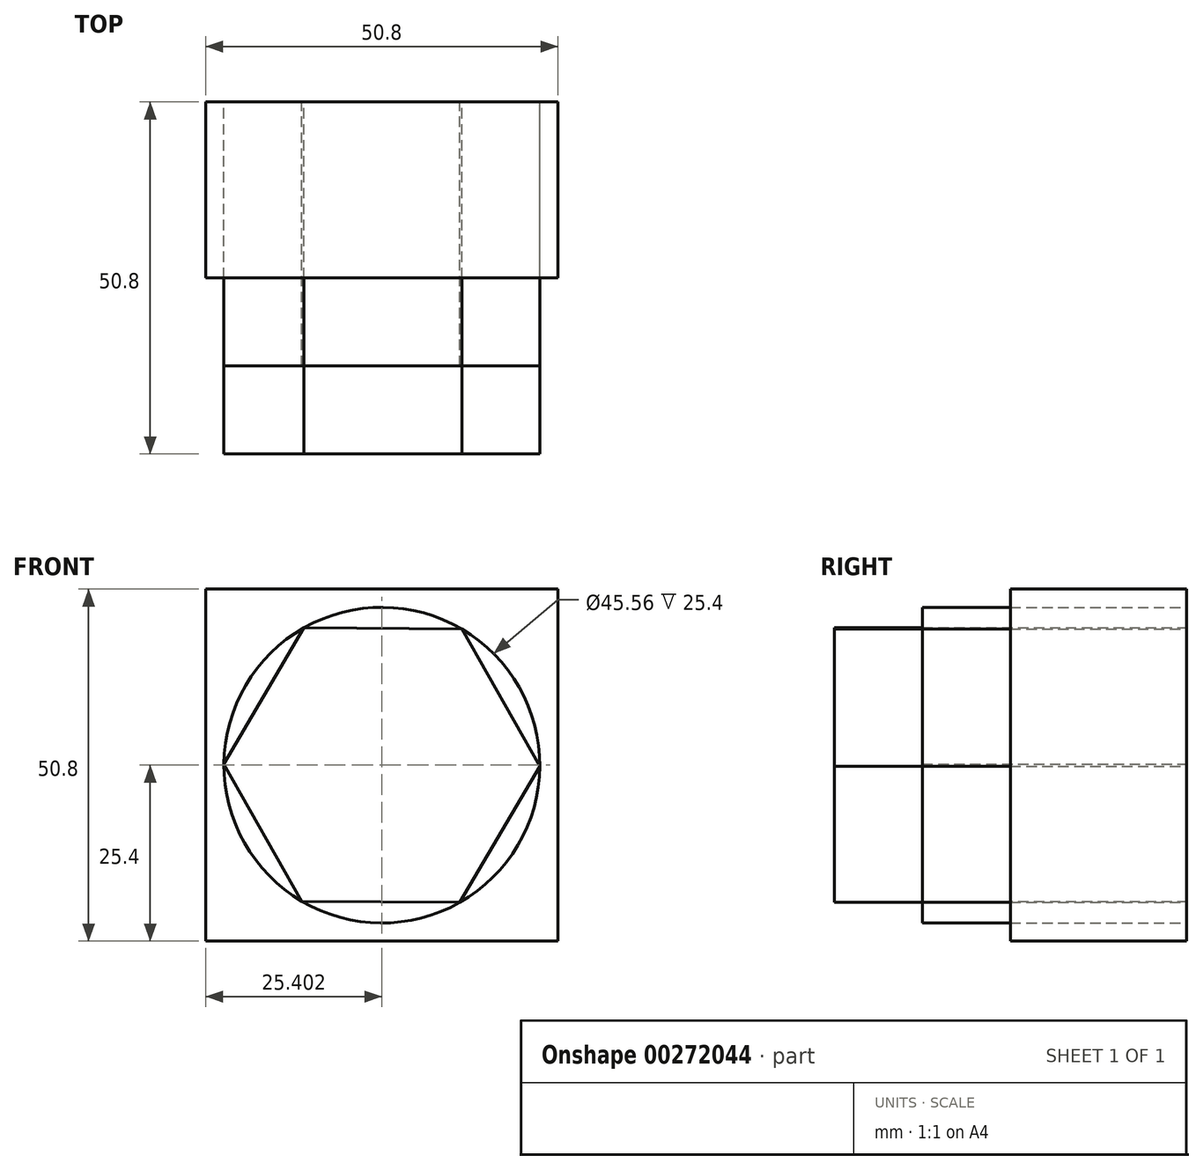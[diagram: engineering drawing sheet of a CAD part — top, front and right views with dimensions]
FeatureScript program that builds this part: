
annotation { "Feature Type Name" : "Feature", "Feature Type Description" : "" }
export const myFeature = defineFeature(function(context is Context, id is Id, definition is map)
    precondition{}
    {
        {
            var Q0;
            Q0=qCreatedBy(makeId("Front.planeOp"),FACE);
            var sketch = newSketch(context, id + "F0", { "sketchPlane" : qUnion([Q0])});
            skLineSegment(sketch, "E0.bottom", {"start": v(-36.5, 21.67) * mm, "end": v(14.3, 21.67) * mm});
            skLineSegment(sketch, "E0.top", {"start": v(-36.5, -29.13) * mm, "end": v(14.3, -29.13) * mm});
            skLineSegment(sketch, "E0.left", {"start": v(-36.5, 21.67) * mm, "end": v(-36.5, -29.13) * mm});
            skLineSegment(sketch, "E0.right", {"start": v(14.3, 21.67) * mm, "end": v(14.3, -29.13) * mm});
            skLineSegment(sketch, "E1", {"start": v(-11.1, 21.67) * mm, "end": v(-11.1, 19.05) * mm});
            skLineSegment(sketch, "E2", {"start": v(-36.5, -3.73) * mm, "end": v(-33.89, -3.73) * mm});
            skCircle(sketch, "E3", {"center": v(-11.1, -3.73) * mm, "radius": 22.78 * mm});
            skLineSegment(sketch, "E4.trimOffspring", {"start": v(-11.1, -26.5) * mm, "end": v(-11.1, -29.13) * mm});
            skLineSegment(sketch, "E5.trimOffspring", {"start": v(11.67, -3.73) * mm, "end": v(14.3, -3.73) * mm});
            skCircle(sketch, "E6.cCircle", {"center": v(-11.1, -3.73) * mm, "radius": 22.78 * mm, "construction": true});
            skLineSegment(sketch, "E6.0", {"start": v(-22.34, 16.09) * mm, "end": v(0.44, 15.9) * mm});
            skLineSegment(sketch, "E6.1", {"start": v(0.44, 15.9) * mm, "end": v(11.67, -3.9) * mm});
            skLineSegment(sketch, "E6.2", {"start": v(11.67, -3.9) * mm, "end": v(0.13, -23.55) * mm});
            skLineSegment(sketch, "E6.3", {"start": v(0.13, -23.55) * mm, "end": v(-22.65, -23.37) * mm});
            skLineSegment(sketch, "E6.4", {"start": v(-22.65, -23.37) * mm, "end": v(-33.89, -3.55) * mm});
            skLineSegment(sketch, "E6.5", {"start": v(-33.89, -3.55) * mm, "end": v(-22.34, 16.09) * mm});
            skSolve(sketch);
        }
        {
            var Q0;
            {var subQ3=sQuery(id+"F0.wireOp",EDGE,"E1");Q0=makeQuery(id+"F0.imprint","IMPRINT",FACE,{"disambiguationData":[TD([[makeQuery(id+"F0.imprint","IMPRINT",EDGE,{"derivedFrom":subQ3}),1.0]])]});}
            var Q1;
            {var subQ1=sQuery(id+"F0.wireOp",EDGE,"E1");Q1=makeQuery(id+"F0.imprint","IMPRINT",FACE,{"disambiguationData":[TD([[makeQuery(id+"F0.imprint","IMPRINT",EDGE,{"derivedFrom":subQ1}),-1.0]])]});}
            var Q2;
            {var subQ1=sQuery(id+"F0.wireOp",EDGE,"E2");Q2=makeQuery(id+"F0.imprint","IMPRINT",FACE,{"disambiguationData":[TD([[makeQuery(id+"F0.imprint","IMPRINT",EDGE,{"derivedFrom":subQ1}),-1.0]])]});}
            var Q3;
            {var subQ8=sQuery(id+"F0.wireOp",EDGE,"E4.trimOffspring");Q3=makeQuery(id+"F0.imprint","IMPRINT",FACE,{"disambiguationData":[TD([[makeQuery(id+"F0.imprint","IMPRINT",EDGE,{"derivedFrom":subQ8}),1.0]])]});}
            extrude(context, id + "F1", {"entities" : qUnion([Q0, Q1, Q2, Q3]), "depth" : 25.4 * mm});
        }
        {
            var Q0;
            Q0=makeQuery(id+"F0.imprint","IMPRINT",FACE,{"disambiguationData":[TD([[makeQuery(id+"F0.imprint","IMPRINT",EDGE,{"derivedFrom":sQuery(id+"F0.wireOp",EDGE,"E6.0")}),-1.0]])]});
            extrude(context, id + "F2", {"entities" : qUnion([Q0]), "operationType" : NewBodyOperationType.ADD, "depth" : 50.8 * mm});
        }
        {
            var Q0;
            {var subQ0=sQuery(id+"F0.wireOp",EDGE,"E6.5");Q0=makeQuery(id+"F0.imprint","IMPRINT",FACE,{"disambiguationData":[TD([[makeQuery(id+"F0.imprint","IMPRINT",EDGE,{"derivedFrom":subQ0}),1.0]])]});}
            var Q1;
            {var subQ2=sQuery(id+"F0.wireOp",EDGE,"E6.1");Q1=makeQuery(id+"F0.imprint","IMPRINT",FACE,{"disambiguationData":[TD([[makeQuery(id+"F0.imprint","IMPRINT",EDGE,{"derivedFrom":subQ2}),1.0]])]});}
            var Q2;
            {var subQ2=sQuery(id+"F0.wireOp",EDGE,"E6.0");Q2=makeQuery(id+"F0.imprint","IMPRINT",FACE,{"disambiguationData":[TD([[makeQuery(id+"F0.imprint","IMPRINT",EDGE,{"derivedFrom":subQ2}),1.0]])]});}
            var Q3;
            {var subQ2=sQuery(id+"F0.wireOp",EDGE,"E6.4");Q3=makeQuery(id+"F0.imprint","IMPRINT",FACE,{"disambiguationData":[TD([[makeQuery(id+"F0.imprint","IMPRINT",EDGE,{"derivedFrom":subQ2}),1.0]])]});}
            var Q4;
            {var subQ2=sQuery(id+"F0.wireOp",EDGE,"E6.3");Q4=makeQuery(id+"F0.imprint","IMPRINT",FACE,{"disambiguationData":[TD([[makeQuery(id+"F0.imprint","IMPRINT",EDGE,{"derivedFrom":subQ2}),1.0]])]});}
            var Q5;
            {var subQ0=sQuery(id+"F0.wireOp",EDGE,"E6.2");Q5=makeQuery(id+"F0.imprint","IMPRINT",FACE,{"disambiguationData":[TD([[makeQuery(id+"F0.imprint","IMPRINT",EDGE,{"derivedFrom":subQ0}),1.0]])]});}
            extrude(context, id + "F3", {"entities" : qUnion([Q0, Q1, Q2, Q3, Q4, Q5]), "depth" : 38.1 * mm});
        }
    });
